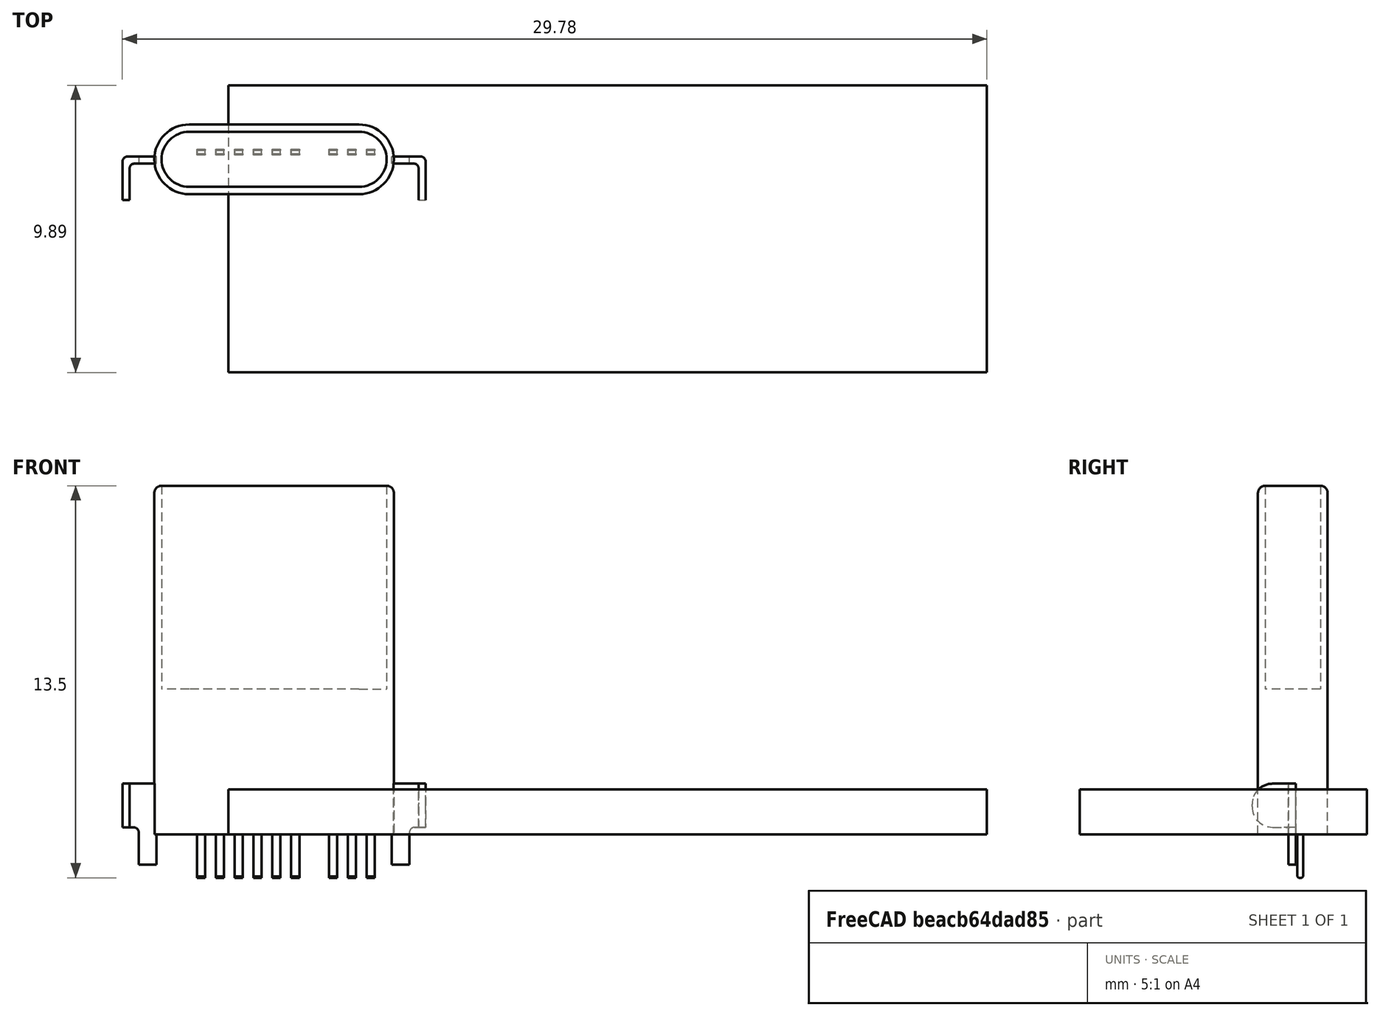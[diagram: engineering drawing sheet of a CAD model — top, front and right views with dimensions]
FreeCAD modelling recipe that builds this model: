
FCSTD DOCUMENT  (FreeCAD 1.0R39109 (Git))
Label: Dual Type-C Connector
License: All rights reserved
LicenseURL: https://en.wikipedia.org/wiki/All_rights_reserved
objects: App::Link×3, App::FeaturePython×3, Part::Feature×1, Sketcher::SketchObject×1, PartDesign::Pad×1, PartDesign::Body×1, Assembly::JointGroup×1, Assembly::AssemblyObject×1, App::DocumentObjectGroup×1
note: 7 computed .brp shape members not serialized (recipe doc carries the construction recipe); baked Part::Feature solids carry a one-line shape summary decoded from their .brp

FEATURE [Part::Feature] Part__Feature  label="Type C Male Connector"
  shape: bbox 10.45 x 2.699 x 13.5 mm, 107 faces (baked)
FEATURE [Sketcher::SketchObject] Sketch
  ArcFitTolerance = 1e-06
  AttachmentSupport = -> [XY_Plane001]
  FullyConstrained = false
  MakeInternals = false
  MapMode = 5
  sketch-geometry (4):
    g0: LineSegment StartX=-1.57833 StartY=2.5515 StartZ=0 EndX=-1.57833 EndY=-7.3385 EndZ=0
    g1: LineSegment StartX=-1.57833 StartY=-7.3385 StartZ=0 EndX=24.5517 EndY=-7.3385 EndZ=0
    g2: LineSegment StartX=24.5517 StartY=-7.3385 StartZ=0 EndX=24.5517 EndY=2.5515 EndZ=0
    g3: LineSegment StartX=24.5517 StartY=2.5515 StartZ=0 EndX=-1.57833 EndY=2.5515 EndZ=0
  constraints (10):
    c: Coincident(g0,g1)
    c: Coincident(g1,g2)
    c: Coincident(g2,g3)
    c: Coincident(g3,g0)
    c: Vertical(g0)
    c: Vertical(g2)
    c: Horizontal(g1)
    c: Horizontal(g3)
    c: DistanceY(g0,g0) = 9.89
    c: DistanceX(g3,g3) = 26.13
FEATURE [PartDesign::Pad] Pad
  Direction = (0,0,1)
  Length = 1.54
  Length2 = 10
  Profile = -> Sketch
  ReferenceAxis = -> Sketch [N_Axis]
  Refine = true
  Suppressed = false
  Type = 0
FEATURE [PartDesign::Body] Body  label="Board"
  AllowCompound = false
  Group = -> [Sketch,Pad]
  Origin = -> Origin001
  Tip = -> Pad
FEATURE [App::Link] Board  label="Board001"
  LinkedObject = -> Body
FEATURE [App::FeaturePython] GroundedJoint  # Assembly grounded joint (typed FeaturePython)
  ObjectToGround = -> Board
FEATURE [App::Link] Type_C_Male_Connector  label="Type C Male Connector001"
  LinkPlacement = pos=(2.73167,-2.3935,1.54) rot=(0,0,1;1.5708rad)
  LinkedObject = -> Part__Feature
  Placement = pos=(2.73167,-2.3935,1.54) rot=(0,0,1;1.5708rad)
FEATURE [App::Link] Type_C_Male_Connector001  label="Type C Male Connector002"
  LinkPlacement = pos=(20.2417,-2.3935,1.54) rot=(0,0,-1;1.5708rad)
  LinkedObject = -> Part__Feature
  Placement = pos=(20.2417,-2.3935,1.54) rot=(0,0,-1;1.5708rad)
FEATURE [App::FeaturePython] Joint  label="Fixed"  # Assembly joint (typed FeaturePython)
  Activated = true
  AngleMax = 0
  AngleMin = 0
  Detach1 = false
  Detach2 = false
  Distance = 0
  Distance2 = 0
  EnableAngleMax = false
  EnableAngleMin = false
  EnableLengthMax = false
  EnableLengthMin = false
  JointType = 0 (Fixed)
  LengthMax = 0
  LengthMin = 0
  Offset2 = pos=(0,0,15.11) rot=(0,0,1;3.14159rad)
  Placement1 = pos=(0,-1.2,5.875) rot=(1,0,0;1.5708rad)
  Placement2 = pos=(0,-16.31,5.875) rot=(0,-0.707107,0.707107;3.14159rad)
  Reference1 = -> Assembly [Type_C_Male_Connector.Face63,Type_C_Male_Connector.Face63]
  Reference2 = -> Assembly [Type_C_Male_Connector001.Face63,Type_C_Male_Connector001.Face63]
FEATURE [App::FeaturePython] Joint001  label="Fixed001"  # Assembly joint (typed FeaturePython)
  Activated = true
  AngleMax = 0
  AngleMin = 0
  Detach1 = false
  Detach2 = false
  Distance = 0
  Distance2 = 0
  EnableAngleMax = false
  EnableAngleMin = false
  EnableLengthMax = false
  EnableLengthMin = false
  JointType = 0 (Fixed)
  LengthMax = 0
  LengthMin = 0
  Offset2 = pos=(0,-5.51,0) rot=(0,0,1;0rad)
  Placement1 = pos=(0,-1.2,0) rot=(0.707107,0,0.707107;3.14159rad)
  Placement2 = pos=(19.0417,-2.3935,1.54) rot=(0.57735,0.57735,0.57735;4.18879rad)
  Reference1 = -> Assembly [Type_C_Male_Connector001.Edge211,Type_C_Male_Connector001.Edge211]
  Reference2 = -> Assembly [Board.Edge10,Board.Edge10]
FEATURE [Assembly::JointGroup] Joints
  Group = -> [GroundedJoint,Joint,Joint001]
FEATURE [Assembly::AssemblyObject] Assembly  label="Full Assembly"
  Group = -> [Joints,Board,GroundedJoint,Type_C_Male_Connector,Type_C_Male_Connector001,Joint,Joint001]
  Origin = -> Origin
  Type = Assembly
FEATURE [App::DocumentObjectGroup] Group  label="Parts"
  Group = -> [Part__Feature,Body]
